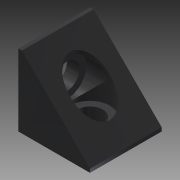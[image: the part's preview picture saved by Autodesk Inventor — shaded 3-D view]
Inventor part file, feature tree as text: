
AUTODESK INVENTOR PART (.ipt)
format: ipt  version: 2014 SP1 (Build 180222100, 222)  size: 113,664 bytes
history: native  units: in
note: dims shown in document units (in); Inventor stores cm internally (conversion verified against a paired STEP export)
features: extrude x5, sketch x5
ambient origin geometry x8: Origin, YZ Plane, XZ Plane, XY Plane, X Axis, Y Axis, Z Axis, Center Point
bodies: Solid1 (feature_tree)
feature tree (10):
  extrude  "Extrusion1"  Depth=0.7874in
  extrude  "Extrusion2"  Depth=0.7874in
  extrude  "Extrusion3"  Depth=0.7874in
  extrude  "Extrusion4"  Depth=0.1378in
  extrude  "Extrusion5"  Depth=0.1378in
  sketch  "Sketch1"  dims[d0=135.0deg d1=0.7874in]
  sketch  "Sketch2"  dims[d2=0.7874in d3=0.0394in]
  sketch  "Sketch3"  dims[d4=0.7874in d5=0.0in d6=0.2811in]
  sketch  "Sketch4"  dims[d7=0.1378in d8=0.0in d9=0.4331in]
  sketch  "Sketch5"  dims[d10=0.1378in d11=0.0in d12=0.2811in d13=0.1378in d14=0.0in d15=0.4331in d16=0.1378in d17=0.0in]
